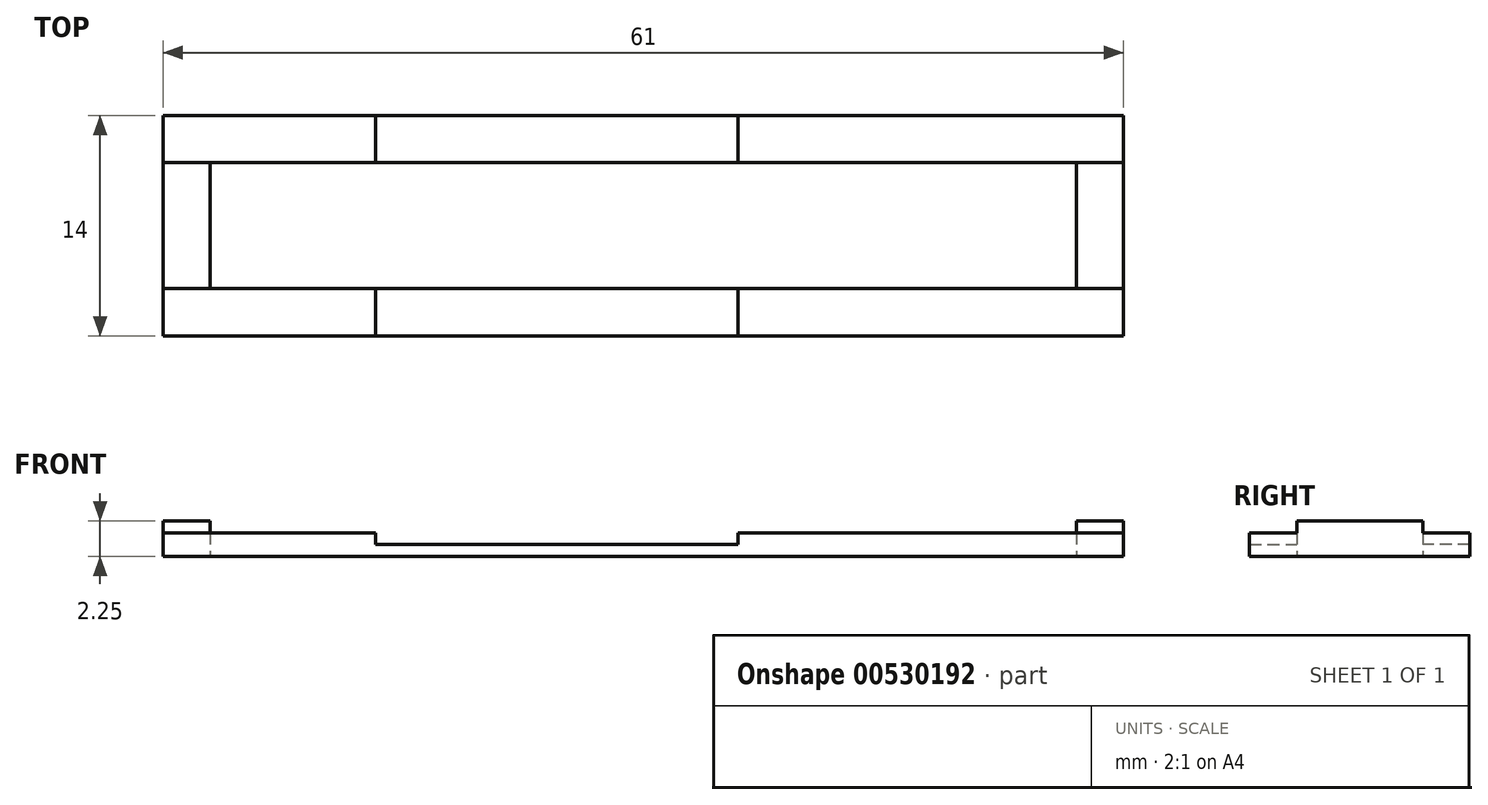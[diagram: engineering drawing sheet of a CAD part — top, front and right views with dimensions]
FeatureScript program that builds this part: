
annotation { "Feature Type Name" : "Feature", "Feature Type Description" : "" }
export const myFeature = defineFeature(function(context is Context, id is Id, definition is map)
    precondition{}
    {
        {
            var Q0;
            Q0=qCreatedBy(makeId("Top.planeOp"),FACE);
            var sketch = newSketch(context, id + "F0", { "sketchPlane" : qUnion([Q0])});
            skLineSegment(sketch, "E0.bottom", {"start": v(30.5, -7) * mm, "end": v(-30.5, -7) * mm});
            skLineSegment(sketch, "E0.top", {"start": v(30.5, 7) * mm, "end": v(-30.5, 7) * mm});
            skLineSegment(sketch, "E0.left", {"start": v(30.5, -7) * mm, "end": v(30.5, 7) * mm});
            skLineSegment(sketch, "E0.right", {"start": v(-30.5, -7) * mm, "end": v(-30.5, 7) * mm});
            skPoint(sketch, "E0.middle", {"position": v(0, 0) * mm});
            skLineSegment(sketch, "E1.bottom", {"start": v(27.5, -4) * mm, "end": v(-27.5, -4) * mm});
            skLineSegment(sketch, "E1.top", {"start": v(27.5, 4) * mm, "end": v(-27.5, 4) * mm});
            skLineSegment(sketch, "E1.left", {"start": v(27.5, -4) * mm, "end": v(27.5, 4) * mm});
            skLineSegment(sketch, "E1.right", {"start": v(-27.5, -4) * mm, "end": v(-27.5, 4) * mm});
            skLineSegment(sketch, "E2", {"start": v(-30.5, 0) * mm, "end": v(-17, 0) * mm, "construction": true});
            skPoint(sketch, "E2.endSnap0", {"position": v(-27.5, 0) * mm});
            skLineSegment(sketch, "E3", {"start": v(30.5, 0) * mm, "end": v(6, 0) * mm, "construction": true});
            skPoint(sketch, "E3.endSnap0", {"position": v(27.5, 0) * mm});
            skLineSegment(sketch, "E4", {"start": v(-17, 4) * mm, "end": v(-17, 7) * mm});
            skLineSegment(sketch, "E5", {"start": v(-17, -4) * mm, "end": v(-17, -7) * mm});
            skLineSegment(sketch, "E6", {"start": v(6, 4) * mm, "end": v(6, 7) * mm});
            skLineSegment(sketch, "E7", {"start": v(6, -4) * mm, "end": v(6, -7) * mm});
            skLineSegment(sketch, "E8.bottom", {"start": v(-30.5, 4.01) * mm, "end": v(-27.5, 4.01) * mm});
            skLineSegment(sketch, "E8.top", {"start": v(-30.5, -4) * mm, "end": v(-27.5, -4) * mm});
            skLineSegment(sketch, "E8.left", {"start": v(-30.5, 4.01) * mm, "end": v(-30.5, -4) * mm});
            skLineSegment(sketch, "E8.right", {"start": v(-27.5, 4.01) * mm, "end": v(-27.5, -4) * mm});
            skLineSegment(sketch, "E9.bottom", {"start": v(27.5, 4) * mm, "end": v(30.5, 4) * mm});
            skLineSegment(sketch, "E9.top", {"start": v(27.5, -4) * mm, "end": v(30.5, -4) * mm});
            skLineSegment(sketch, "E9.left", {"start": v(27.5, 4) * mm, "end": v(27.5, -4) * mm});
            skLineSegment(sketch, "E9.right", {"start": v(30.5, 4) * mm, "end": v(30.5, -4) * mm});
            skSolve(sketch);
        }
        {
            var Q0;
            {var subQ0=sQuery(id+"F0.wireOp",EDGE,"E0.left");Q0=makeQuery(id+"F0.imprint","IMPRINT",FACE,{"disambiguationData":[TD([[makeQuery(id+"F0.imprint","IMPRINT",EDGE,{"derivedFrom":subQ0}),1.0]])]});}
            var Q1;
            {var subQ0=sQuery(id+"F0.wireOp",EDGE,"E4");Q1=makeQuery(id+"F0.imprint","IMPRINT",FACE,{"disambiguationData":[TD([[makeQuery(id+"F0.imprint","IMPRINT",EDGE,{"derivedFrom":subQ0}),-1.0]])]});}
            var Q2;
            {var subQ3=sQuery(id+"F0.wireOp",EDGE,"E0.right");Q2=makeQuery(id+"F0.imprint","IMPRINT",FACE,{"disambiguationData":[TD([[makeQuery(id+"F0.imprint","IMPRINT",EDGE,{"derivedFrom":subQ3}),-1.0]])]});}
            var Q3;
            {var subQ0=sQuery(id+"F0.wireOp",EDGE,"E5");Q3=makeQuery(id+"F0.imprint","IMPRINT",FACE,{"disambiguationData":[TD([[makeQuery(id+"F0.imprint","IMPRINT",EDGE,{"derivedFrom":subQ0}),1.0]])]});}
            var Q4;
            {var subQ0=sQuery(id+"F0.wireOp",EDGE,"E4");Q4=makeQuery(id+"F0.imprint","IMPRINT",FACE,{"disambiguationData":[TD([[makeQuery(id+"F0.imprint","IMPRINT",EDGE,{"derivedFrom":subQ0}),1.0]])]});}
            var Q5;
            {var subQ2=sQuery(id+"F0.wireOp",EDGE,"E8.bottom");Q5=makeQuery(id+"F0.imprint","IMPRINT",FACE,{"disambiguationData":[TD([[makeQuery(id+"F0.imprint","IMPRINT",EDGE,{"derivedFrom":subQ2}),-1.0]])]});}
            var Q6;
            Q6=makeQuery(id+"F0.imprint","IMPRINT",FACE,{"disambiguationData":[TD([[makeQuery(id+"F0.imprint","IMPRINT",EDGE,{"derivedFrom":sQuery(id+"F0.wireOp",EDGE,"E9.bottom")}),-1.0]])]});
            extrude(context, id + "F1", {"entities" : qUnion([Q0, Q1, Q2, Q3, Q4, Q5, Q6]), "depth" : .75 * mm, "offsetDistance" : 25 * mm});
        }
        {
            var Q0;
            {var subQ2=sQuery(id+"F0.wireOp",EDGE,"E8.bottom");Q0=makeQuery(id+"F0.imprint","IMPRINT",FACE,{"disambiguationData":[TD([[makeQuery(id+"F0.imprint","IMPRINT",EDGE,{"derivedFrom":subQ2}),-1.0]])]});}
            var Q1;
            Q1=makeQuery(id+"F0.imprint","IMPRINT",FACE,{"disambiguationData":[TD([[makeQuery(id+"F0.imprint","IMPRINT",EDGE,{"derivedFrom":sQuery(id+"F0.wireOp",EDGE,"E9.bottom")}),-1.0]])]});
            extrude(context, id + "F2", {"entities" : qUnion([Q0, Q1]), "operationType" : NewBodyOperationType.ADD, "depth" : 2.25 * mm, "offsetDistance" : 25 * mm});
        }
        {
            var Q0;
            {var subQ0=sQuery(id+"F0.wireOp",EDGE,"E4");Q0=makeQuery(id+"F0.imprint","IMPRINT",FACE,{"disambiguationData":[TD([[makeQuery(id+"F0.imprint","IMPRINT",EDGE,{"derivedFrom":subQ0}),1.0]])]});}
            var Q1;
            {var subQ4=sQuery(id+"F0.wireOp",EDGE,"E6");Q1=makeQuery(id+"F0.imprint","IMPRINT",FACE,{"disambiguationData":[TD([[makeQuery(id+"F0.imprint","IMPRINT",EDGE,{"derivedFrom":subQ4}),-1.0]])]});}
            var Q2;
            {var subQ0=sQuery(id+"F0.wireOp",EDGE,"E7");Q2=makeQuery(id+"F0.imprint","IMPRINT",FACE,{"disambiguationData":[TD([[makeQuery(id+"F0.imprint","IMPRINT",EDGE,{"derivedFrom":subQ0}),1.0]])]});}
            var Q3;
            {var subQ4=sQuery(id+"F0.wireOp",EDGE,"E5");Q3=makeQuery(id+"F0.imprint","IMPRINT",FACE,{"disambiguationData":[TD([[makeQuery(id+"F0.imprint","IMPRINT",EDGE,{"derivedFrom":subQ4}),-1.0]])]});}
            var Q4;
            {var subQ2=sQuery(id+"F0.wireOp",EDGE,"E8.bottom");Q4=makeQuery(id+"F0.imprint","IMPRINT",FACE,{"disambiguationData":[TD([[makeQuery(id+"F0.imprint","IMPRINT",EDGE,{"derivedFrom":subQ2}),-1.0]])]});}
            var Q5;
            Q5=makeQuery(id+"F0.imprint","IMPRINT",FACE,{"disambiguationData":[TD([[makeQuery(id+"F0.imprint","IMPRINT",EDGE,{"derivedFrom":sQuery(id+"F0.wireOp",EDGE,"E9.bottom")}),-1.0]])]});
            extrude(context, id + "F3", {"entities" : qUnion([Q0, Q1, Q2, Q3, Q4, Q5]), "operationType" : NewBodyOperationType.ADD, "depth" : 1.5 * mm, "offsetDistance" : 25 * mm});
        }
    });
